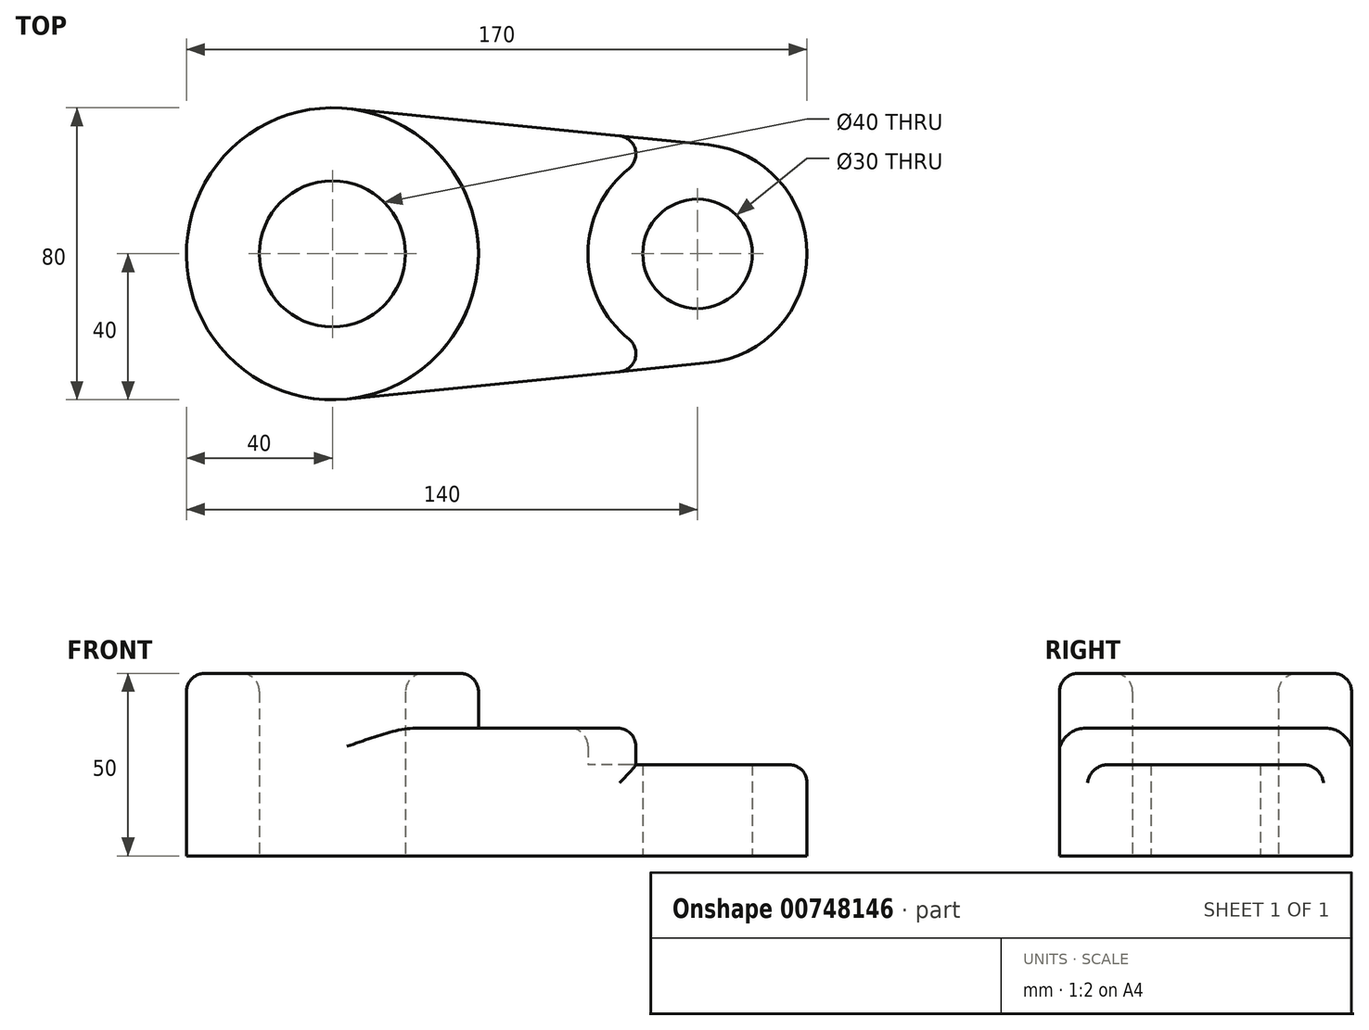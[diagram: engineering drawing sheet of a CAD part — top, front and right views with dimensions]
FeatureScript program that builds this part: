
annotation { "Feature Type Name" : "Feature", "Feature Type Description" : "" }
export const myFeature = defineFeature(function(context is Context, id is Id, definition is map)
    precondition{}
    {
        {
            var Q0;
            Q0=qCreatedBy(makeId("Top.planeOp"),FACE);
            var sketch = newSketch(context, id + "F0", { "sketchPlane" : qUnion([Q0])});
            skCircle(sketch, "E0", {"center": v(-50, 0) * mm, "radius": 20 * mm});
            skCircle(sketch, "E1", {"center": v(-50, 0) * mm, "radius": 40 * mm});
            skCircle(sketch, "E2", {"center": v(50, 0) * mm, "radius": 15 * mm});
            skCircle(sketch, "E3", {"center": v(50, 0) * mm, "radius": 30 * mm});
            skLineSegment(sketch, "E4", {"start": v(-46, 39.8) * mm, "end": v(53, 29.85) * mm});
            skLineSegment(sketch, "E5", {"start": v(-46, -39.8) * mm, "end": v(53, -29.85) * mm});
            skSolve(sketch);
        }
        {
            var Q0;
            Q0=makeQuery(id+"F0.imprint","IMPRINT",FACE,{"disambiguationData":[TD([[makeQuery(id+"F0.imprint","IMPRINT",EDGE,{"derivedFrom":sQuery(id+"F0.wireOp",EDGE,"E0")}),-1.0]])]});
            extrude(context, id + "F1", {"entities" : qUnion([Q0]), "depth" : 50 * mm, "offsetDistance" : 25 * mm});
        }
        {
            var Q0;
            {var subQ0=sQuery(id+"F0.wireOp",EDGE,"E4");Q0=makeQuery(id+"F0.imprint","IMPRINT",FACE,{"disambiguationData":[TD([[makeQuery(id+"F0.imprint","IMPRINT",EDGE,{"derivedFrom":subQ0}),-1.0]])]});}
            extrude(context, id + "F2", {"entities" : qUnion([Q0]), "operationType" : NewBodyOperationType.ADD, "depth" : 35 * mm, "offsetDistance" : 25 * mm});
        }
        {
            var Q0;
            Q0=makeQuery(id+"F0.imprint","IMPRINT",FACE,{"disambiguationData":[TD([[makeQuery(id+"F0.imprint","IMPRINT",EDGE,{"derivedFrom":sQuery(id+"F0.wireOp",EDGE,"E2")}),-1.0]])]});
            extrude(context, id + "F3", {"entities" : qUnion([Q0]), "operationType" : NewBodyOperationType.ADD, "depth" : 25 * mm, "offsetDistance" : 25 * mm});
        }
        {
            var Q0;
            Q0=makeQuery(id+"F1.opExtrude","CAP_FACE",FACE,{"disambiguationData":[OSD([sQuery(id+"F0.wireOp",EDGE,"E0"),sQuery(id+"F0.wireOp",EDGE,"E1")])],"isStart":false});
            var Q1;
            Q1=makeQuery(id+"F2.opExtrude","CAP_EDGE",EDGE,{"disambiguationData":[OSD([sQuery(id+"F0.wireOp",EDGE,"E1")])],"isStart":false});
            var Q2;
            Q2=makeQuery(id+"F2.opExtrude","CAP_EDGE",EDGE,{"disambiguationData":[OSD([sQuery(id+"F0.wireOp",EDGE,"E3")])],"isStart":false});
            var Q3;
            {var subQ0=sQuery(id+"F0.wireOp",EDGE,"E5");var subQ1=sQuery(id+"F0.wireOp",EDGE,"E3");Q3=makeQuery(id+"F3.boolean.opBoolean","SPLIT",EDGE,{"disambiguationData":[topologyDisambiguationEdgeConnected([makeQuery(id+"F3.opExtrude","SWEPT_FACE",FACE,{"disambiguationData":[OSD([subQ1])]})])],"derivedFrom":makeQuery(id+"F2.opExtrude","SWEPT_EDGE",EDGE,{"disambiguationData":[OSD([subQ1,subQ0])]})});}
            var Q4;
            {var subQ0=sQuery(id+"F0.wireOp",EDGE,"E4");var subQ1=sQuery(id+"F0.wireOp",EDGE,"E3");Q4=makeQuery(id+"F3.boolean.opBoolean","SPLIT",EDGE,{"disambiguationData":[topologyDisambiguationEdgeConnected([makeQuery(id+"F3.opExtrude","SWEPT_FACE",FACE,{"disambiguationData":[OSD([subQ1])]})])],"derivedFrom":makeQuery(id+"F2.opExtrude","SWEPT_EDGE",EDGE,{"disambiguationData":[OSD([subQ1,subQ0])]})});}
            var Q5;
            {var subQ0=sQuery(id+"F0.wireOp",EDGE,"E3");Q5=makeQuery(id+"F3.boolean.opBoolean","SPLIT",EDGE,{"disambiguationData":[topologyDisambiguationEdgeConnected([makeQuery(id+"F3.opExtrude","SWEPT_FACE",FACE,{"disambiguationData":[OSD([subQ0])]})])],"derivedFrom":makeQuery(id+"F3.opExtrude","CAP_EDGE",EDGE,{"disambiguationData":[OSD([subQ0])],"isStart":false})});}
            fillet(context, id + "F4", {"entities" : qUnion([Q0, Q1, Q2, Q3, Q4, Q5]), "radius" : 5 * mm, "tangentPropagation" : true, "allowEdgeOverflow" : false});
        }
        {
            var Q0;
            Q0=makeQuery(id+"F2.opExtrude","CAP_EDGE",EDGE,{"disambiguationData":[OSD([sQuery(id+"F0.wireOp",EDGE,"E5")])],"isStart":false});
            var Q1;
            Q1=makeQuery(id+"F2.opExtrude","CAP_EDGE",EDGE,{"disambiguationData":[OSD([sQuery(id+"F0.wireOp",EDGE,"E4")])],"isStart":false});
            fillet(context, id + "F5", {"entities" : qUnion([Q0, Q1]), "radius" : 5 * mm, "tangentPropagation" : true, "allowEdgeOverflow" : false});
        }
    });
